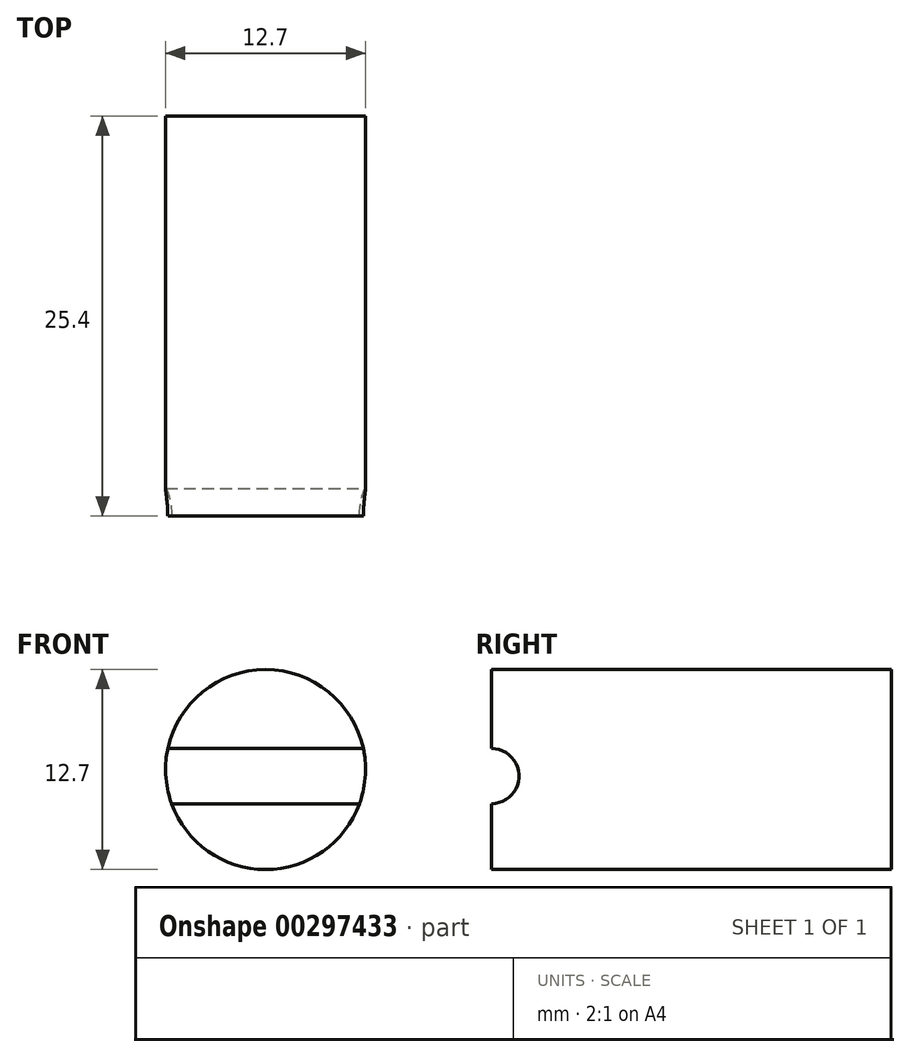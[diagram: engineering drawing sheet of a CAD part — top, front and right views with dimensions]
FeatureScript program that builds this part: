
annotation { "Feature Type Name" : "Feature", "Feature Type Description" : "" }
export const myFeature = defineFeature(function(context is Context, id is Id, definition is map)
    precondition{}
    {
        {
            var Q0;
            Q0=qCreatedBy(makeId("Front.planeOp"),FACE);
            var sketch = newSketch(context, id + "F0", { "sketchPlane" : qUnion([Q0])});
            skCircle(sketch, "E0", {"center": v(0, 0.42) * mm, "radius": 6.35 * mm});
            skSolve(sketch);
        }
        {
            var Q0;
            Q0 = qSketchRegion(id + "F0", true);
            extrude(context, id + "F1", {"entities" : qUnion([Q0]), "oppositeDirection" : true, "depth" : 25.4 * mm});
        }
        {
            var Q0;
            Q0=qCreatedBy(makeId("Right.planeOp"),FACE);
            var sketch = newSketch(context, id + "F2", { "sketchPlane" : qUnion([Q0])});
            skCircle(sketch, "E1", {"center": v(0, 0) * mm, "radius": 1.75 * mm});
            skSolve(sketch);
        }
        {
            var Q0;
            Q0 = qSketchRegion(id + "F2", true);
            extrude(context, id + "F3", {"entities" : qUnion([Q0]), "operationType" : NewBodyOperationType.REMOVE, "endBound" : BoundingType.SYMMETRIC, "oppositeDirection" : true, "depth" : 25.4 * mm});
        }
    });
